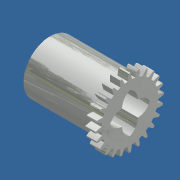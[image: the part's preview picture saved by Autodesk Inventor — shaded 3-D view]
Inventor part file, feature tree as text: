
AUTODESK INVENTOR PART (.ipt)
format: ipt  version: 2020 (Build 240168000, 168)  size: 1,658,368 bytes
history: mixed  units: mm
features: extrude x4, sketch x4, fillet x1, imported_body x1
ambient origin geometry x8: Origin, YZ Plane, XZ Plane, XY Plane, X Axis, Y Axis, Z Axis, Center Point
bodies: Solid1 (imported_parasolid)
feature tree (10):
  fillet  "Redondeo6"  Radius=1.0mm
  extrude  "Extrusion1"  Depth=30.0mm TaperAngle=0.0deg
  extrude  "Extrusion4"  Depth=5.0mm
  extrude  "Extrusion5"  Depth=2.0mm
  extrude  "Extrusion6"  Depth=40.25mm TaperAngle=0.0deg
  sketch  "Sketch1"  dims[d4=4.0mm d5=0.0mm d8=30.0mm d9=0.0mm]
  sketch  "Sketch4"  dims[d10=8.5mm d11=5.0mm]
  sketch  "Sketch5"  dims[d12=2.0mm d13=3.0mm]
  sketch  "Sketch7"  dims[d14=40.0mm d16=360.0deg d18=40.25mm d19=0.0mm d20=20.0mm d21=4.0mm d22=0.0mm]
  imported_body  NMx_Import_Brep_tag  [imported B-rep: ~20 faces, bbox_mm=[30.4, 18.513162, 17.682576]]
